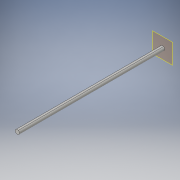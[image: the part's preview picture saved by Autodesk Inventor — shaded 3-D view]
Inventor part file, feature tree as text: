
AUTODESK INVENTOR PART (.ipt)
format: ipt  version: 2016 (Build 200138000, 138)  size: 103,424 bytes
history: native  units: in
note: dims shown in document units (in); Inventor stores cm internally (conversion verified against a paired STEP export)
features: other x3, plane x1, extrude x1, sketch x1
ambient origin geometry x8: Origin, YZ Plane, XZ Plane, XY Plane, X Axis, Y Axis, Z Axis, Center Point
bodies: Body1 (feature_tree)
feature tree (6):
  other  "FRONT"
  other  "TOP"
  other  "RIGHT"
  plane  "Work Plane4"
  extrude  "Extrusion1"  [1 undecoded]
  sketch  "Sketch1"  dims[d0=6.2992in d1=0.0in]
note: 1 required parameter value undecoded (feature->parameter linkage not recoverable at this tier; creation-order binding heuristic only, values carry confidence <= 0.55)
